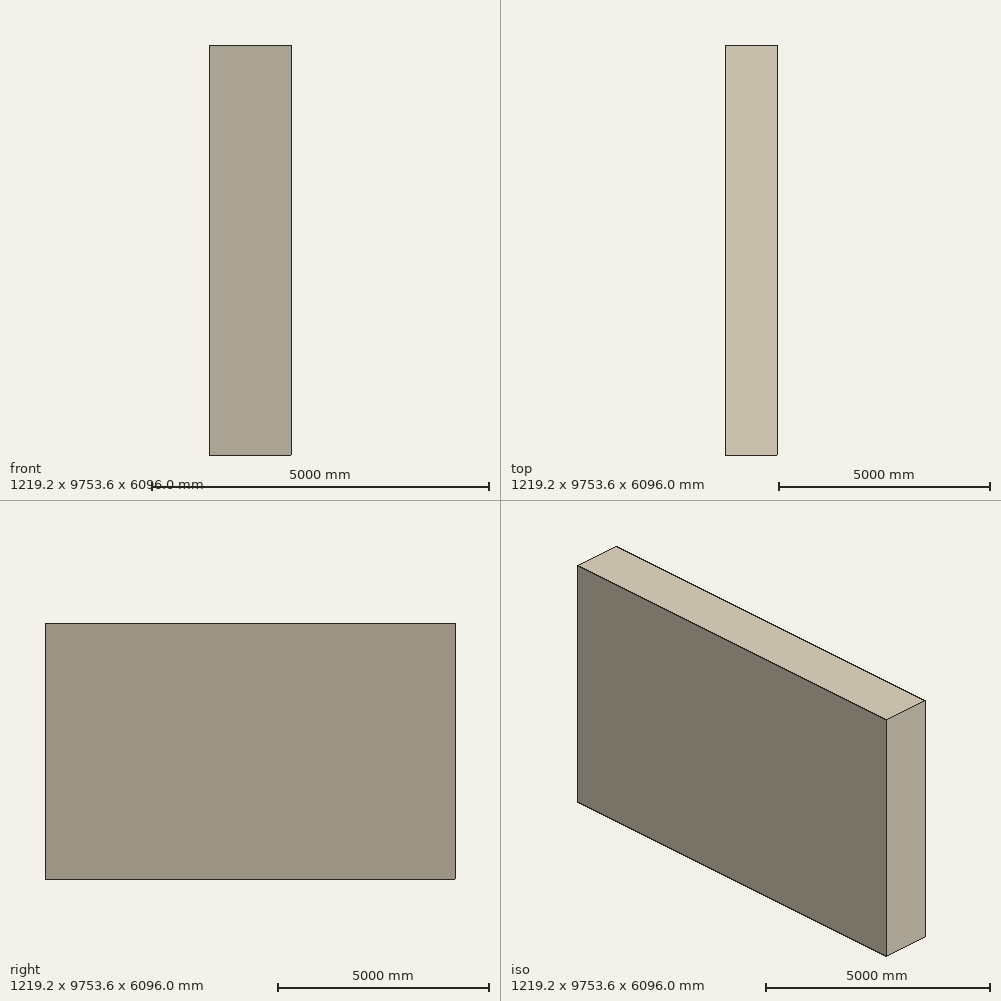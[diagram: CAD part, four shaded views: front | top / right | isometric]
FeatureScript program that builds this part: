
annotation { "Feature Type Name" : "Feature", "Feature Type Description" : "" }
export const myFeature = defineFeature(function(context is Context, id is Id, definition is map)
    precondition{}
    {
        {
            var Q0;
            Q0=qCreatedBy(makeId("Right.planeOp"),FACE);
            var sketch = newSketch(context, id + "F0", { "sketchPlane" : qUnion([Q0])});
            skLineSegment(sketch, "E0.bottom", {"start": v(4876.8, -3048) * mm, "end": v(-4876.8, -3048) * mm});
            skLineSegment(sketch, "E0.top", {"start": v(4876.8, 3048) * mm, "end": v(-4876.8, 3048) * mm});
            skLineSegment(sketch, "E0.left", {"start": v(4876.8, -3048) * mm, "end": v(4876.8, 3048) * mm});
            skLineSegment(sketch, "E0.right", {"start": v(-4876.8, -3048) * mm, "end": v(-4876.8, 3048) * mm});
            skPoint(sketch, "E0.middle", {"position": v(0, 0) * mm});
            skSolve(sketch);
        }
        {
            var Q0;
            Q0=makeQuery(id+"F0.imprint","IMPRINT",FACE,{"disambiguationData":[TD([[makeQuery(id+"F0.imprint","IMPRINT",EDGE,{"derivedFrom":sQuery(id+"F0.wireOp",EDGE,"E0.bottom")}),-1.0]])]});
            extrude(context, id + "F1", {"entities" : qUnion([Q0]), "depth" : 1219.2 * mm, "offsetDistance" : 30.48 * mm});
        }
    });
